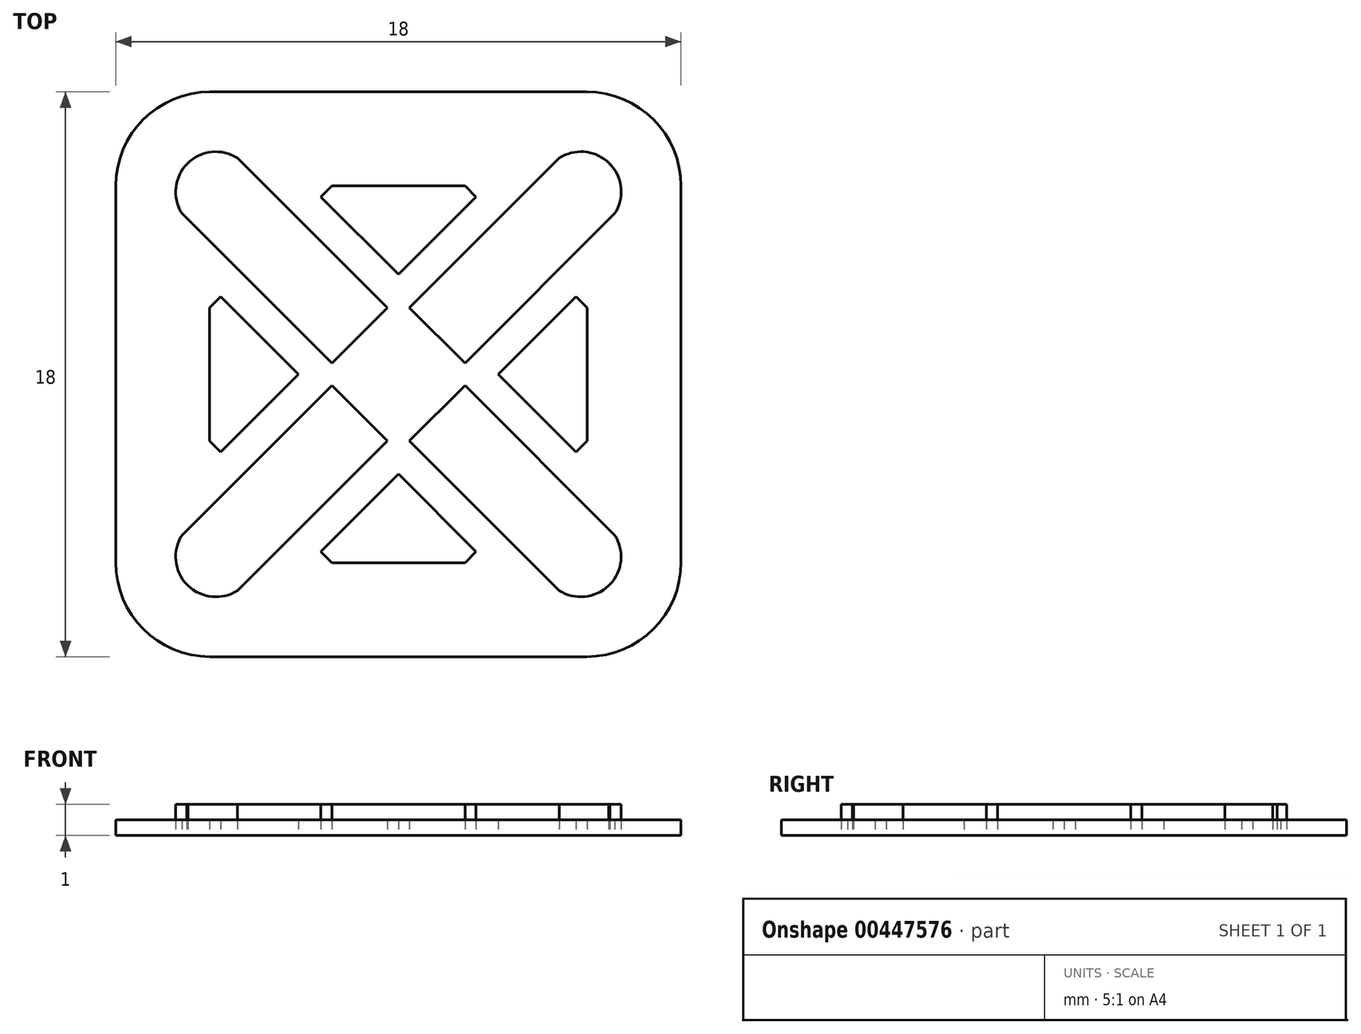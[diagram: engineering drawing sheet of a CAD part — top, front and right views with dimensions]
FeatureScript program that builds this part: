
annotation { "Feature Type Name" : "Feature", "Feature Type Description" : "" }
export const myFeature = defineFeature(function(context is Context, id is Id, definition is map)
    precondition{}
    {
        {
            var Q0;
            Q0=qCreatedBy(makeId("Top.planeOp"),FACE);
            var sketch = newSketch(context, id + "F0", { "sketchPlane" : qUnion([Q0])});
            skLineSegment(sketch, "E0.bottom", {"start": v(6, -9) * mm, "end": v(-6, -9) * mm});
            skLineSegment(sketch, "E0.top", {"start": v(6, 9) * mm, "end": v(-6, 9) * mm});
            skLineSegment(sketch, "E0.left", {"start": v(9, -6) * mm, "end": v(9, 6) * mm});
            skLineSegment(sketch, "E0.right", {"start": v(-9, -6) * mm, "end": v(-9, 6) * mm});
            skLineSegment(sketch, "E1", {"start": v(-9, 9) * mm, "end": v(9, -9) * mm, "construction": true});
            skLineSegment(sketch, "E2", {"start": v(9, 9) * mm, "end": v(-9, -9) * mm, "construction": true});
            skPoint(sketch, "E3.visualSharp", {"position": v(-9, 9) * mm});
            skArc(sketch, "E3.filletArc", {"start": v(-6, 9) * mm, "mid": v(-8.12, 8.12) * mm, "end": v(-9, 6) * mm});
            skPoint(sketch, "E4.visualSharp", {"position": v(9, 9) * mm});
            skArc(sketch, "E4.filletArc", {"start": v(9, 6) * mm, "mid": v(8.12, 8.12) * mm, "end": v(6, 9) * mm});
            skPoint(sketch, "E5.visualSharp", {"position": v(9, -9) * mm});
            skArc(sketch, "E5.filletArc", {"start": v(6, -9) * mm, "mid": v(8.12, -8.12) * mm, "end": v(9, -6) * mm});
            skPoint(sketch, "E6.visualSharp", {"position": v(-9, -9) * mm});
            skArc(sketch, "E6.filletArc", {"start": v(-9, -6) * mm, "mid": v(-8.12, -8.12) * mm, "end": v(-6, -9) * mm});
            skLineSegment(sketch, "E7", {"start": v(-6.9, 5.13) * mm, "end": v(-2.12, 0.35) * mm});
            skLineSegment(sketch, "E8", {"start": v(6.7, -6.74) * mm, "end": v(6.74, -6.7) * mm});
            skLineSegment(sketch, "E9", {"start": v(6.9, -5.13) * mm, "end": v(1.77, 0) * mm});
            skLineSegment(sketch, "E10", {"start": v(5.13, 6.9) * mm, "end": v(0.35, 2.12) * mm});
            skLineSegment(sketch, "E11", {"start": v(-6.74, -6.7) * mm, "end": v(-6.7, -6.74) * mm});
            skLineSegment(sketch, "E12", {"start": v(-5.13, -6.9) * mm, "end": v(-0.35, -2.12) * mm});
            skLineSegment(sketch, "E13", {"start": v(6.8, 6.64) * mm, "end": v(6.64, 6.8) * mm});
            skLineSegment(sketch, "E14", {"start": v(-0.35, 2.12) * mm, "end": v(-2.12, 0.35) * mm});
            skLineSegment(sketch, "E15", {"start": v(-2.12, -0.35) * mm, "end": v(-0.35, -2.12) * mm});
            skLineSegment(sketch, "E16", {"start": v(0.35, -2.12) * mm, "end": v(2.12, -0.35) * mm});
            skLineSegment(sketch, "E17", {"start": v(2.12, 0.35) * mm, "end": v(0.35, 2.12) * mm});
            skLineSegment(sketch, "E18.trimOffspring", {"start": v(-0.35, 2.12) * mm, "end": v(-5.13, 6.9) * mm});
            skLineSegment(sketch, "E19.trimOffspring", {"start": v(0.35, -2.12) * mm, "end": v(5.13, -6.9) * mm});
            skLineSegment(sketch, "E20.trimOffspring", {"start": v(-2.12, -0.35) * mm, "end": v(-6.9, -5.13) * mm});
            skLineSegment(sketch, "E21.trimOffspring", {"start": v(2.12, 0.35) * mm, "end": v(6.9, 5.13) * mm});
            skArc(sketch, "E22", {"start": v(-5.13, 6.9) * mm, "mid": v(-6.72, 6.72) * mm, "end": v(-6.9, 5.13) * mm});
            skArc(sketch, "E23", {"start": v(6.9, 5.13) * mm, "mid": v(6.72, 6.72) * mm, "end": v(5.13, 6.9) * mm});
            skArc(sketch, "E24", {"start": v(5.13, -6.9) * mm, "mid": v(6.72, -6.72) * mm, "end": v(6.9, -5.13) * mm});
            skArc(sketch, "E25", {"start": v(-6.9, -5.13) * mm, "mid": v(-6.72, -6.72) * mm, "end": v(-5.13, -6.9) * mm});
            skLineSegment(sketch, "E26", {"start": v(-10.24, -7.06) * mm, "end": v(7.17, 10.35) * mm, "construction": true});
            skLineSegment(sketch, "E27", {"start": v(-6.94, 10.12) * mm, "end": v(10.72, -7.54) * mm, "construction": true});
            skLineSegment(sketch, "E28", {"start": v(11.17, 7.99) * mm, "end": v(-7.66, -10.84) * mm, "construction": true});
            skLineSegment(sketch, "E29", {"start": v(-10.72, 7.54) * mm, "end": v(7.18, -10.36) * mm, "construction": true});
            skLineSegment(sketch, "E30", {"start": v(-3.18, 0) * mm, "end": v(-5.66, -2.48) * mm});
            skLineSegment(sketch, "E31", {"start": v(-5.66, -2.48) * mm, "end": v(-6, -2.12) * mm});
            skLineSegment(sketch, "E32", {"start": v(-6, -2.12) * mm, "end": v(-6, 2.12) * mm});
            skLineSegment(sketch, "E33", {"start": v(-6, 2.12) * mm, "end": v(-5.66, 2.47) * mm});
            skLineSegment(sketch, "E34", {"start": v(-5.66, 2.47) * mm, "end": v(-3.18, 0) * mm});
            skLineSegment(sketch, "E35", {"start": v(0, 3.18) * mm, "end": v(2.48, 5.66) * mm});
            skLineSegment(sketch, "E36", {"start": v(2.48, 5.66) * mm, "end": v(2.12, 6) * mm});
            skLineSegment(sketch, "E37", {"start": v(2.12, 6) * mm, "end": v(-2.12, 6) * mm});
            skLineSegment(sketch, "E38", {"start": v(-2.12, 6) * mm, "end": v(-2.47, 5.66) * mm});
            skLineSegment(sketch, "E39", {"start": v(-2.47, 5.66) * mm, "end": v(0, 3.18) * mm});
            skLineSegment(sketch, "E40", {"start": v(3.18, 0) * mm, "end": v(5.66, -2.48) * mm});
            skLineSegment(sketch, "E41", {"start": v(5.66, -2.48) * mm, "end": v(6.01, -2.12) * mm});
            skLineSegment(sketch, "E42", {"start": v(6.01, -2.12) * mm, "end": v(6.01, 2.12) * mm});
            skLineSegment(sketch, "E43", {"start": v(6.01, 2.12) * mm, "end": v(5.66, 2.47) * mm});
            skLineSegment(sketch, "E44", {"start": v(5.66, 2.47) * mm, "end": v(3.18, 0) * mm});
            skLineSegment(sketch, "E45", {"start": v(0, -3.18) * mm, "end": v(-2.47, -5.66) * mm});
            skLineSegment(sketch, "E46", {"start": v(-2.47, -5.66) * mm, "end": v(-2.12, -6.01) * mm});
            skLineSegment(sketch, "E47", {"start": v(-2.12, -6.01) * mm, "end": v(2.12, -6.01) * mm});
            skLineSegment(sketch, "E48", {"start": v(2.12, -6.01) * mm, "end": v(2.48, -5.66) * mm});
            skLineSegment(sketch, "E49", {"start": v(2.48, -5.66) * mm, "end": v(0, -3.18) * mm});
            skSolve(sketch);
        }
        {
            var Q0;
            Q0=makeQuery(id+"F0.imprint","IMPRINT",FACE,{"disambiguationData":[TD([[makeQuery(id+"F0.imprint","IMPRINT",EDGE,{"derivedFrom":sQuery(id+"F0.wireOp",EDGE,"E7")}),1.0]])]});
            var Q1;
            Q1=makeQuery(id+"F0.imprint","IMPRINT",FACE,{"disambiguationData":[TD([[makeQuery(id+"F0.imprint","IMPRINT",EDGE,{"derivedFrom":sQuery(id+"F0.wireOp",EDGE,"E30")}),-1.0]])]});
            var Q2;
            Q2=makeQuery(id+"F0.imprint","IMPRINT",FACE,{"disambiguationData":[TD([[makeQuery(id+"F0.imprint","IMPRINT",EDGE,{"derivedFrom":sQuery(id+"F0.wireOp",EDGE,"E35")}),1.0]])]});
            var Q3;
            {var subQ2=sQuery(id+"F0.wireOp",EDGE,"E10");Q3=makeQuery(id+"F0.imprint","IMPRINT",FACE,{"disambiguationData":[TD([[makeQuery(id+"F0.imprint","IMPRINT",EDGE,{"derivedFrom":subQ2}),1.0]])]});}
            var Q4;
            Q4=makeQuery(id+"F0.imprint","IMPRINT",FACE,{"disambiguationData":[TD([[makeQuery(id+"F0.imprint","IMPRINT",EDGE,{"derivedFrom":sQuery(id+"F0.wireOp",EDGE,"E40")}),1.0]])]});
            var Q5;
            {var subQ3=sQuery(id+"F0.wireOp",EDGE,"E16");Q5=makeQuery(id+"F0.imprint","IMPRINT",FACE,{"disambiguationData":[TD([[makeQuery(id+"F0.imprint","IMPRINT",EDGE,{"derivedFrom":subQ3}),-1.0]])]});}
            var Q6;
            Q6=makeQuery(id+"F0.imprint","IMPRINT",FACE,{"disambiguationData":[TD([[makeQuery(id+"F0.imprint","IMPRINT",EDGE,{"derivedFrom":sQuery(id+"F0.wireOp",EDGE,"E45")}),1.0]])]});
            var Q7;
            {var subQ3=sQuery(id+"F0.wireOp",EDGE,"E12");Q7=makeQuery(id+"F0.imprint","IMPRINT",FACE,{"disambiguationData":[TD([[makeQuery(id+"F0.imprint","IMPRINT",EDGE,{"derivedFrom":subQ3}),1.0]])]});}
            extrude(context, id + "F1", {"entities" : qUnion([Q0, Q1, Q2, Q3, Q4, Q5, Q6, Q7]), "depth" : 1 * mm});
        }
        {
            var Q0;
            Q0=makeQuery(id+"F0.imprint","IMPRINT",FACE,{"disambiguationData":[TD([[makeQuery(id+"F0.imprint","IMPRINT",EDGE,{"derivedFrom":sQuery(id+"F0.wireOp",EDGE,"E0.bottom")}),-1.0]])]});
            extrude(context, id + "F2", {"entities" : qUnion([Q0]), "depth" : .5 * mm});
        }
    });
